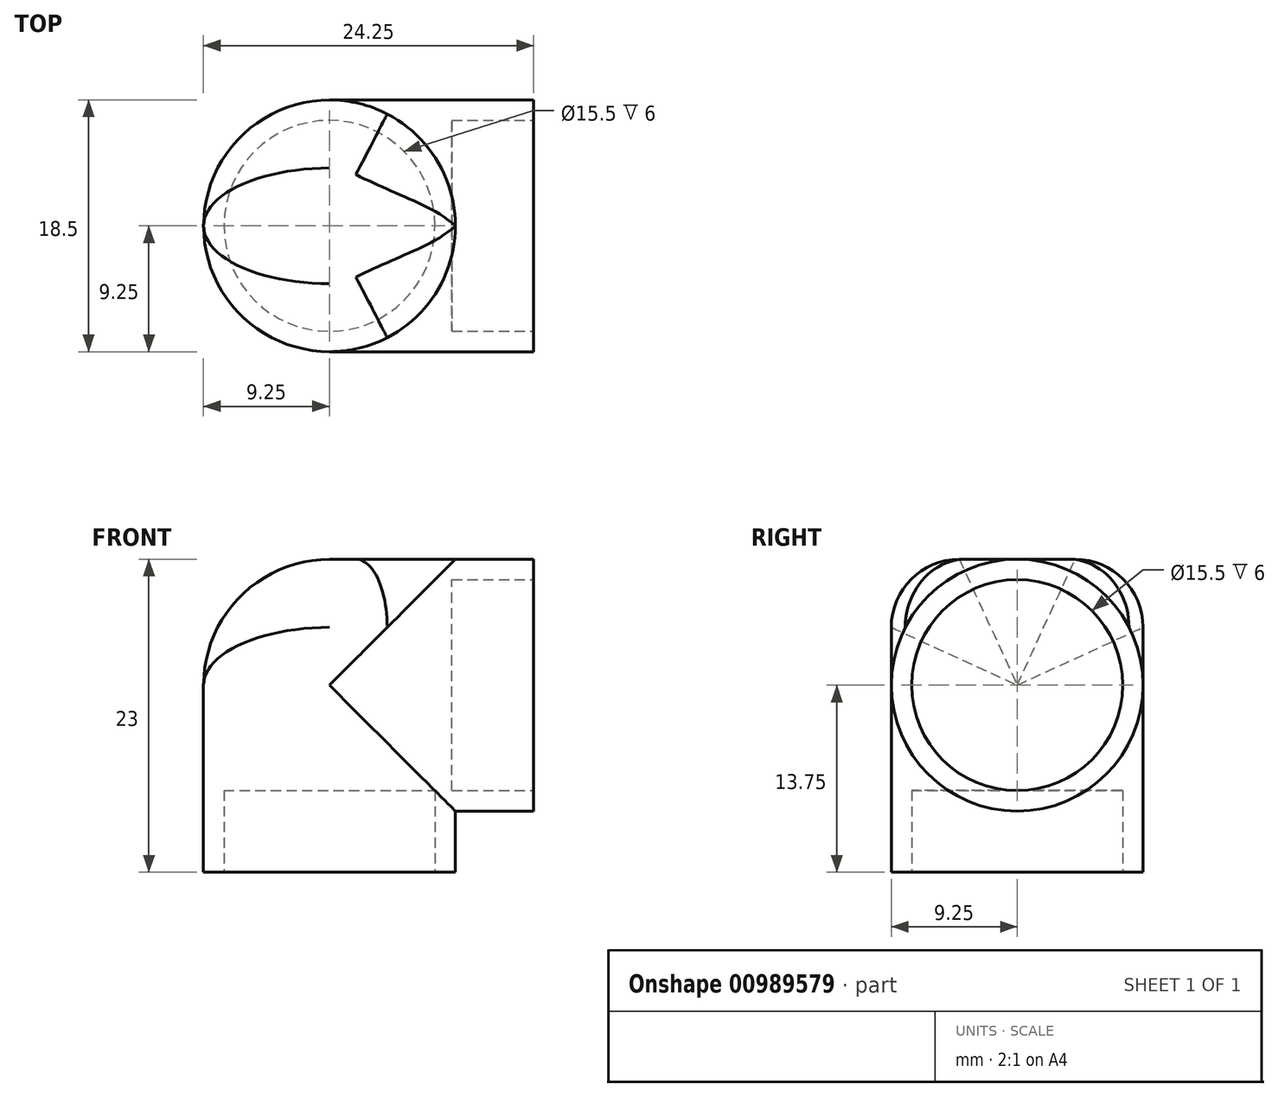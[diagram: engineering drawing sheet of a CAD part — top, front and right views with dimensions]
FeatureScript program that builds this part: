
annotation { "Feature Type Name" : "Feature", "Feature Type Description" : "" }
export const myFeature = defineFeature(function(context is Context, id is Id, definition is map)
    precondition{}
    {
        {
            var Q0;
            Q0=qCreatedBy(makeId("Front.planeOp"),FACE);
            var sketch = newSketch(context, id + "F0", { "sketchPlane" : qUnion([Q0])});
            skLineSegment(sketch, "E0.bottom", {"start": v(0, 0) * mm, "end": v(15, 0) * mm});
            skLineSegment(sketch, "E0.top", {"start": v(0, 9.25) * mm, "end": v(15, 9.25) * mm});
            skLineSegment(sketch, "E0.left", {"start": v(0, 0) * mm, "end": v(0, 9.25) * mm});
            skLineSegment(sketch, "E0.right", {"start": v(15, 0) * mm, "end": v(15, 9.25) * mm});
            skSolve(sketch);
        }
        {
            var Q0;
            Q0=makeQuery(id+"F0.imprint","IMPRINT",FACE,{"disambiguationData":[TD([[makeQuery(id+"F0.imprint","IMPRINT",EDGE,{"derivedFrom":sQuery(id+"F0.wireOp",EDGE,"E0.bottom")}),1.0]])]});
            var Q1;
            Q1=sQuery(id+"F0.wireOp",EDGE,"E0.bottom");
            revolve(context, id + "F1", {"surfaceOperationType" : NewSurfaceOperationType.NEW, "entities" : qUnion([Q0]), "axis" : qUnion([Q1]), "revolveType" : RevolveType.FULL});
        }
        {
            var Q0;
            Q0=qCreatedBy(makeId("Front.planeOp"),FACE);
            var sketch = newSketch(context, id + "F2", { "sketchPlane" : qUnion([Q0])});
            skLineSegment(sketch, "E1.bottom", {"start": v(0, 9.25) * mm, "end": v(-9.25, 9.25) * mm});
            skLineSegment(sketch, "E1.top", {"start": v(0, -13.75) * mm, "end": v(-9.25, -13.75) * mm});
            skLineSegment(sketch, "E1.left", {"start": v(0, 9.25) * mm, "end": v(0, -13.75) * mm});
            skLineSegment(sketch, "E1.right", {"start": v(-9.25, 9.25) * mm, "end": v(-9.25, -13.75) * mm});
            skSolve(sketch);
        }
        {
            var Q0;
            Q0 = qSketchRegion(id + "F2", true);
            var Q1;
            Q1=sQuery(id+"F2.wireOp",EDGE,"E1.left");
            revolve(context, id + "F3", {"operationType" : NewBodyOperationType.ADD, "surfaceOperationType" : NewSurfaceOperationType.NEW, "entities" : qUnion([Q0]), "axis" : qUnion([Q1]), "revolveType" : RevolveType.FULL});
        }
        {
            var Q0;
            Q0=qCreatedBy(makeId("Front.planeOp"),FACE);
            var sketch = newSketch(context, id + "F4", { "sketchPlane" : qUnion([Q0])});
            skLineSegment(sketch, "E2.0", {"start": v(-9.25, 9.25) * mm, "end": v(0, 9.25) * mm});
            skArc(sketch, "E3", {"start": v(0, 9.25) * mm, "mid": v(-6.54, 6.54) * mm, "end": v(-9.25, 0) * mm});
            skLineSegment(sketch, "E4", {"start": v(-9.25, 0) * mm, "end": v(-9.25, 9.25) * mm});
            skSolve(sketch);
        }
        {
            var Q0;
            Q0 = qSketchRegion(id + "F4", true);
            extrude(context, id + "F5", {"entities" : qUnion([Q0]), "operationType" : NewBodyOperationType.REMOVE, "oppositeDirection" : true, "depth" : 25 * mm, "offsetDistance" : 25 * mm, "symmetric" : true});
        }
        {
            var Q0;
            Q0=makeQuery(id+"F5.boolean.opBoolean","INTERSECT",EDGE,{"disambiguationData":[OD(0.0)],"derivedFrom":[makeQuery(id+"F3.opRevolve","SWEPT_FACE",FACE,{"disambiguationData":[OSD([sQuery(id+"F2.wireOp",EDGE,"E1.right")])]}),makeQuery(id+"F5.opExtrude","SWEPT_FACE",FACE,{"disambiguationData":[OSD([sQuery(id+"F4.wireOp",EDGE,"E3")])]})]});
            fillet(context, id + "F6", {"entities" : qUnion([Q0]), "radius" : 5 * mm, "tangentPropagation" : true, "allowEdgeOverflow" : false});
        }
        {
            var Q0;
            Q0=makeQuery(id+"F1.opRevolve","SWEPT_FACE",FACE,{"disambiguationData":[OSD([sQuery(id+"F0.wireOp",EDGE,"E0.right")])]});
            var sketch = newSketch(context, id + "F7", { "sketchPlane" : qUnion([Q0])});
            skCircle(sketch, "E5", {"center": v(0, 0) * mm, "radius": 7.75 * mm});
            skSolve(sketch);
        }
        {
            var Q0;
            Q0 = qSketchRegion(id + "F7", true);
            extrude(context, id + "F8", {"entities" : qUnion([Q0]), "operationType" : NewBodyOperationType.REMOVE, "oppositeDirection" : true, "depth" : 6 * mm, "offsetDistance" : 25 * mm});
        }
        {
            var Q0;
            Q0=makeQuery(id+"F3.opRevolve","SWEPT_FACE",FACE,{"disambiguationData":[OSD([sQuery(id+"F2.wireOp",EDGE,"E1.top")])]});
            var sketch = newSketch(context, id + "F9", { "sketchPlane" : qUnion([Q0])});
            skCircle(sketch, "E6", {"center": v(0, 0) * mm, "radius": 7.75 * mm});
            skSolve(sketch);
        }
        {
            var Q0;
            Q0 = qSketchRegion(id + "F9", true);
            extrude(context, id + "F10", {"entities" : qUnion([Q0]), "operationType" : NewBodyOperationType.REMOVE, "oppositeDirection" : true, "depth" : 6 * mm, "offsetDistance" : 25 * mm});
        }
    });
